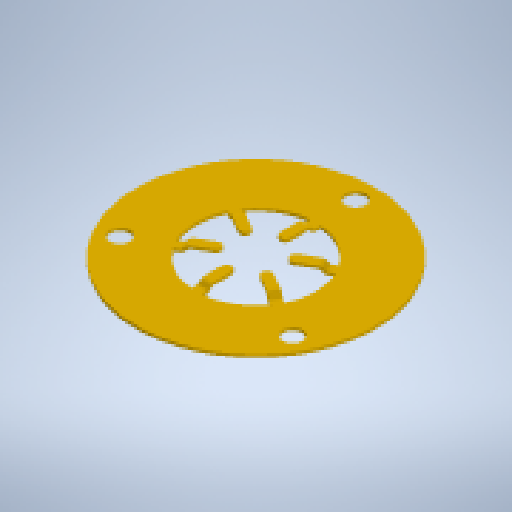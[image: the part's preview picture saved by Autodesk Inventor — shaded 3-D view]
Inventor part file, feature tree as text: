
AUTODESK INVENTOR PART (.ipt)
format: ipt  version: 2023 (Build 270158000, 158)  size: 270,848 bytes
history: native  units: mm
features: sheet_metal_op x9, sketch x4, other x4, chamfer x1, pattern_circular x1
ambient origin geometry x8: Origin, YZ Plane, XZ Plane, XY Plane, X Axis, Y Axis, Z Axis, Center Point
bodies: Body1 (feature_tree)
feature tree (19):
  sheet_metal_op  "Face1"
  sheet_metal_op  "Face2"
  sheet_metal_op  "Flange1"
  sheet_metal_op  "Flange2"
  chamfer  "Corner Round1"
  pattern_circular  "Circular Pattern1"  Count=3 Angle=360.0deg
  sketch  "Sketch1"  dims[d0=24.0mm]
  other  "Plate1"
  sketch  "Sketch2"  dims[d1=2.0mm]
  other  "Plate2"
  sheet_metal_op  "Bend1"
  sketch  "Sketch3"  dims[d2=10.0mm d3=30.0mm d5=360.0deg]
  other  "Plate3"
  sheet_metal_op  "Bend2"
  sheet_metal_op  "Corner1"
  sketch  "Sketch4"  dims[d7=16.0mm d8=1.5mm d9=3.4mm d16=0.3mm d17=5.5mm d18=3.0mm d19=1.0mm d20=0.3mm d21=0.3mm d22=0.15mm d23=0.6mm d24=0.3mm d25=0.3mm d26=0.15mm d27=0.6mm d28=0.3mm d29=0.5mm d30=45.0deg d31=0.3mm d32=1.2mm d33=0.3mm d34=0.3mm d35=0.3mm d36=0.15mm d37=0.6mm d38=0.3mm d39=2.5mm d40=45.0deg d41=0.3mm d42=1.2mm d43=0.3mm d44=0.3mm d45=0.5mm d46=60.0mm d47=360.0deg]
  other  "Plate4"
  sheet_metal_op  "Bend3"
  sheet_metal_op  "Corner2"
